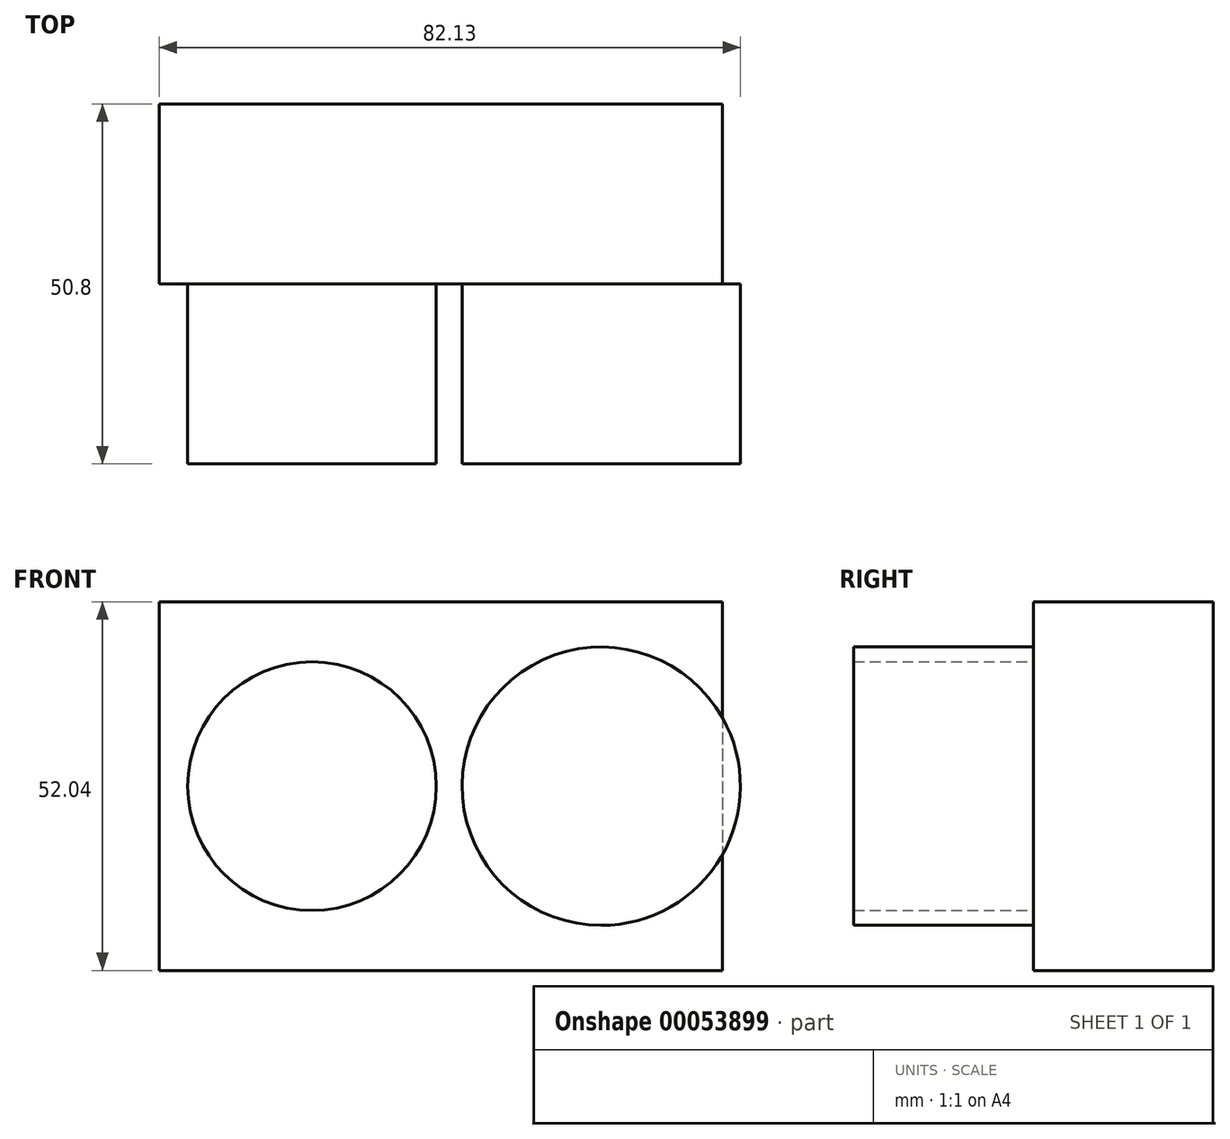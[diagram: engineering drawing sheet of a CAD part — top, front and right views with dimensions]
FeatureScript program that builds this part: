
annotation { "Feature Type Name" : "Feature", "Feature Type Description" : "" }
export const myFeature = defineFeature(function(context is Context, id is Id, definition is map)
    precondition{}
    {
        {
            var Q0;
            Q0=qCreatedBy(makeId("Front.planeOp"),FACE);
            var sketch = newSketch(context, id + "F0", { "sketchPlane" : qUnion([Q0])});
            skLineSegment(sketch, "E0.rect.bottom", {"start": v(39.8, 26.02) * mm, "end": v(-39.8, 26.02) * mm});
            skLineSegment(sketch, "E0.rect.top", {"start": v(39.8, -26.02) * mm, "end": v(-39.8, -26.02) * mm});
            skLineSegment(sketch, "E0.rect.left", {"start": v(39.8, 26.02) * mm, "end": v(39.8, -26.02) * mm});
            skLineSegment(sketch, "E0.rect.right", {"start": v(-39.8, 26.02) * mm, "end": v(-39.8, -26.02) * mm});
            skPoint(sketch, "E0.rect.middle", {"position": v(0, 0) * mm});
            skSolve(sketch);
        }
        {
            var Q0;
            Q0=makeQuery(id+"F0.imprint","IMPRINT",FACE,{"disambiguationData":[TD([[makeQuery(id+"F0.imprint","IMPRINT",EDGE,{"derivedFrom":sQuery(id+"F0.wireOp",EDGE,"E0.rect.bottom")}),1.0]])]});
            extrude(context, id + "F1", {"entities" : qUnion([Q0]), "depth" : 25.4 * mm, "symmetric" : true});
        }
        {
            var Q0;
            Q0=makeQuery(id+"F1.opExtrude","CAP_FACE",FACE,{"disambiguationData":[OSD([sQuery(id+"F0.wireOp",EDGE,"E0.rect.bottom"),sQuery(id+"F0.wireOp",EDGE,"E0.rect.top"),sQuery(id+"F0.wireOp",EDGE,"E0.rect.left"),sQuery(id+"F0.wireOp",EDGE,"E0.rect.right")])],"isStart":false});
            var sketch = newSketch(context, id + "F2", { "sketchPlane" : qUnion([Q0])});
            skCircle(sketch, "E1", {"center": v(22.68, 0) * mm, "radius": 19.66 * mm});
            skCircle(sketch, "E2", {"center": v(-18.18, 0) * mm, "radius": 17.56 * mm});
            skSolve(sketch);
        }
        {
            var Q0;
            Q0 = qSketchRegion(id + "F2", true);
            extrude(context, id + "F3", {"entities" : qUnion([Q0]), "operationType" : NewBodyOperationType.ADD, "depth" : 25.4 * mm});
        }
    });
